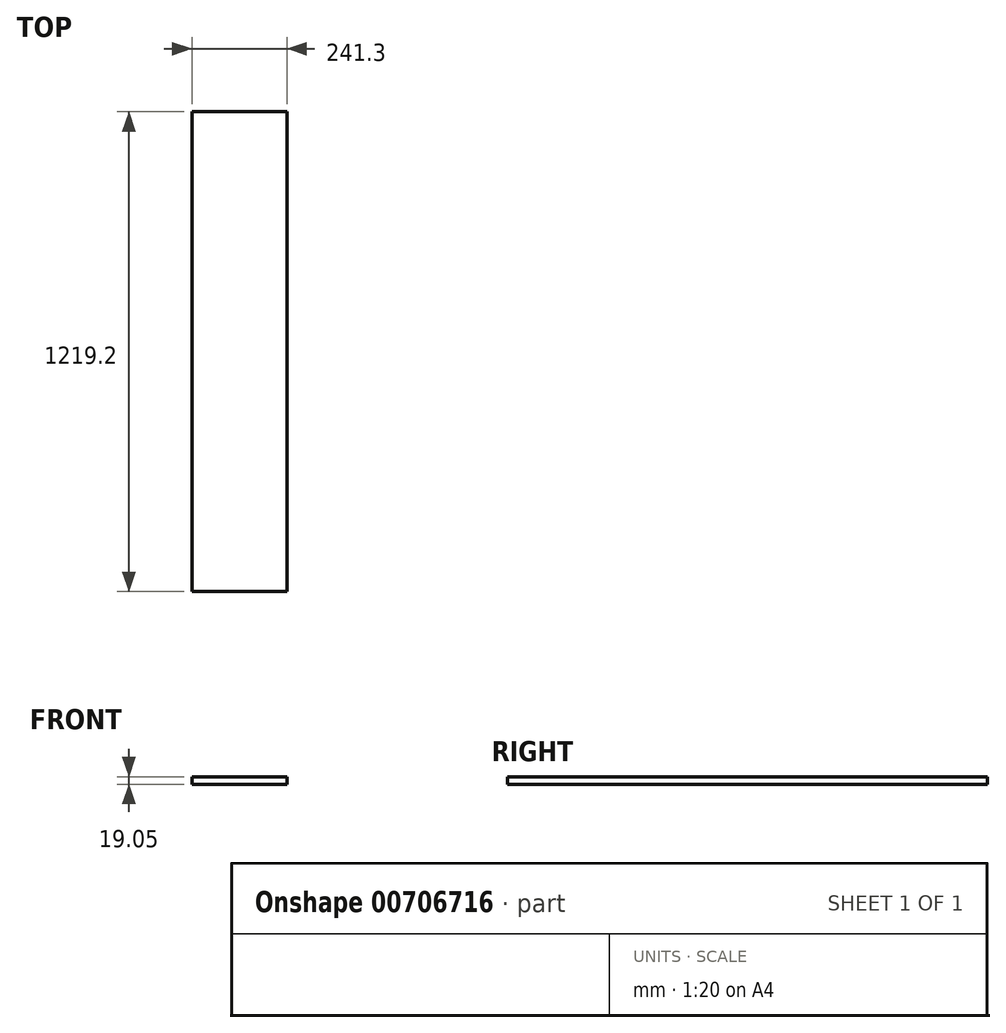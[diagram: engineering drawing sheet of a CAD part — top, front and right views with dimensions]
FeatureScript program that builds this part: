
annotation { "Feature Type Name" : "Feature", "Feature Type Description" : "" }
export const myFeature = defineFeature(function(context is Context, id is Id, definition is map)
    precondition{}
    {
        {
            var Q0;
            Q0=qCreatedBy(makeId("Top.planeOp"),FACE);
            var sketch = newSketch(context, id + "F0", { "sketchPlane" : qUnion([Q0])});
            skLineSegment(sketch, "E0.bottom", {"start": v(0, 0) * mm, "end": v(241.3, 0) * mm});
            skLineSegment(sketch, "E0.top", {"start": v(0, 1219.2) * mm, "end": v(241.3, 1219.2) * mm});
            skLineSegment(sketch, "E0.left", {"start": v(0, 0) * mm, "end": v(0, 1219.2) * mm});
            skLineSegment(sketch, "E0.right", {"start": v(241.3, 0) * mm, "end": v(241.3, 1219.2) * mm});
            skSolve(sketch);
        }
        {
            var Q0;
            Q0=makeQuery(id+"F0.imprint","IMPRINT",FACE,{"disambiguationData":[TD([[makeQuery(id+"F0.imprint","IMPRINT",EDGE,{"derivedFrom":sQuery(id+"F0.wireOp",EDGE,"E0.bottom")}),1.0]])]});
            extrude(context, id + "F1", {"entities" : qUnion([Q0]), "depth" : 19.05 * mm, "offsetDistance" : 25.4 * mm});
        }
    });
